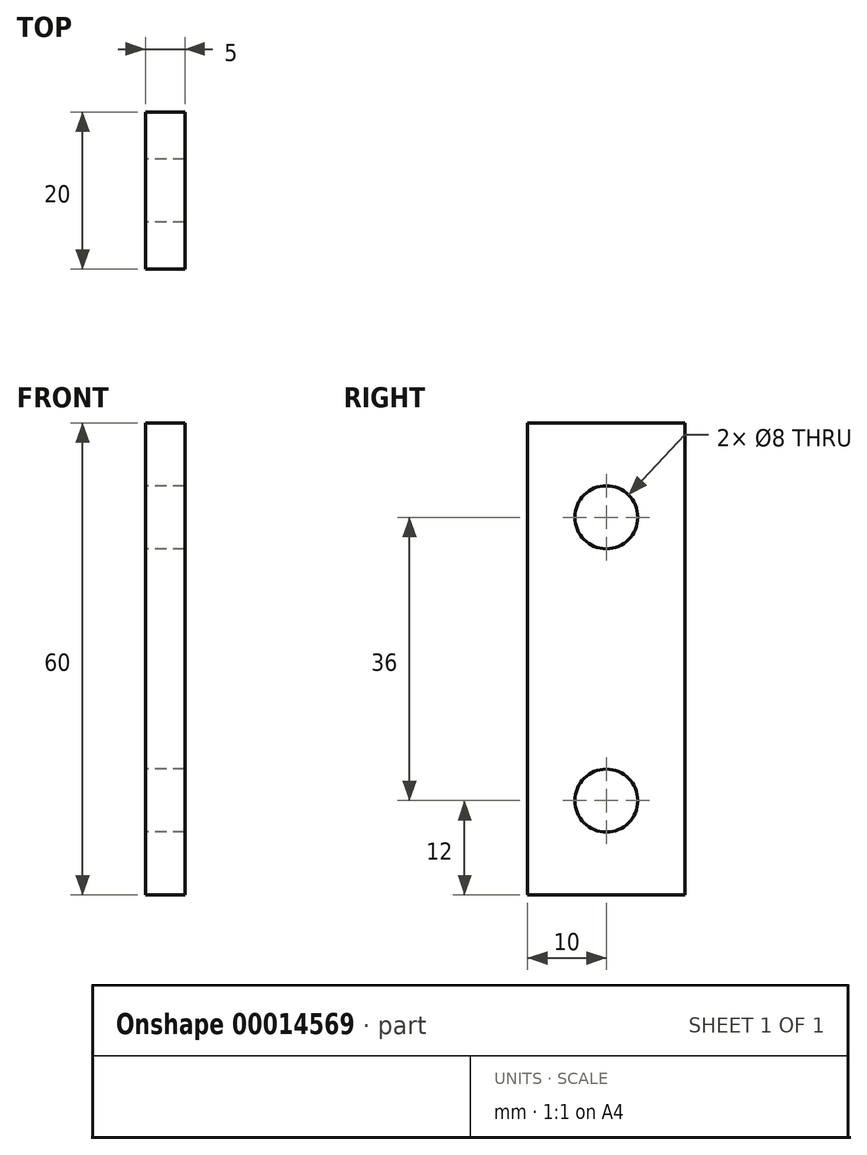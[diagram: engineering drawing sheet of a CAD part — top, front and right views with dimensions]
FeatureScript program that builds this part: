
annotation { "Feature Type Name" : "Feature", "Feature Type Description" : "" }
export const myFeature = defineFeature(function(context is Context, id is Id, definition is map)
    precondition{}
    {
        {
            var Q0;
            Q0=qCreatedBy(makeId("Right.planeOp"),FACE);
            var sketch = newSketch(context, id + "F0", { "sketchPlane" : qUnion([Q0])});
            skLineSegment(sketch, "E0.rect.bottom", {"start": v(-10, 30) * mm, "end": v(10, 30) * mm});
            skLineSegment(sketch, "E0.rect.top", {"start": v(-10, -30) * mm, "end": v(10, -30) * mm});
            skLineSegment(sketch, "E0.rect.left", {"start": v(-10, 30) * mm, "end": v(-10, -30) * mm});
            skLineSegment(sketch, "E0.rect.right", {"start": v(10, 30) * mm, "end": v(10, -30) * mm});
            skPoint(sketch, "E0.rect.middle", {"position": v(0, 0) * mm});
            skLineSegment(sketch, "E1", {"start": v(0, 18) * mm, "end": v(0, -18) * mm, "construction": true});
            skLineSegment(sketch, "E2", {"start": v(-13.22, 0) * mm, "end": v(9.63, 0) * mm, "construction": true});
            skCircle(sketch, "E3", {"center": v(0, 18) * mm, "radius": 4 * mm});
            skCircle(sketch, "E4", {"center": v(0, -18) * mm, "radius": 4 * mm});
            skSolve(sketch);
        }
        {
            var Q0;
            Q0=qSketchRegion(id+"F0",true);
            extrude(context, id + "F1", {"entities" : qUnion([Q0]), "depth" : 5 * mm});
        }
    });
